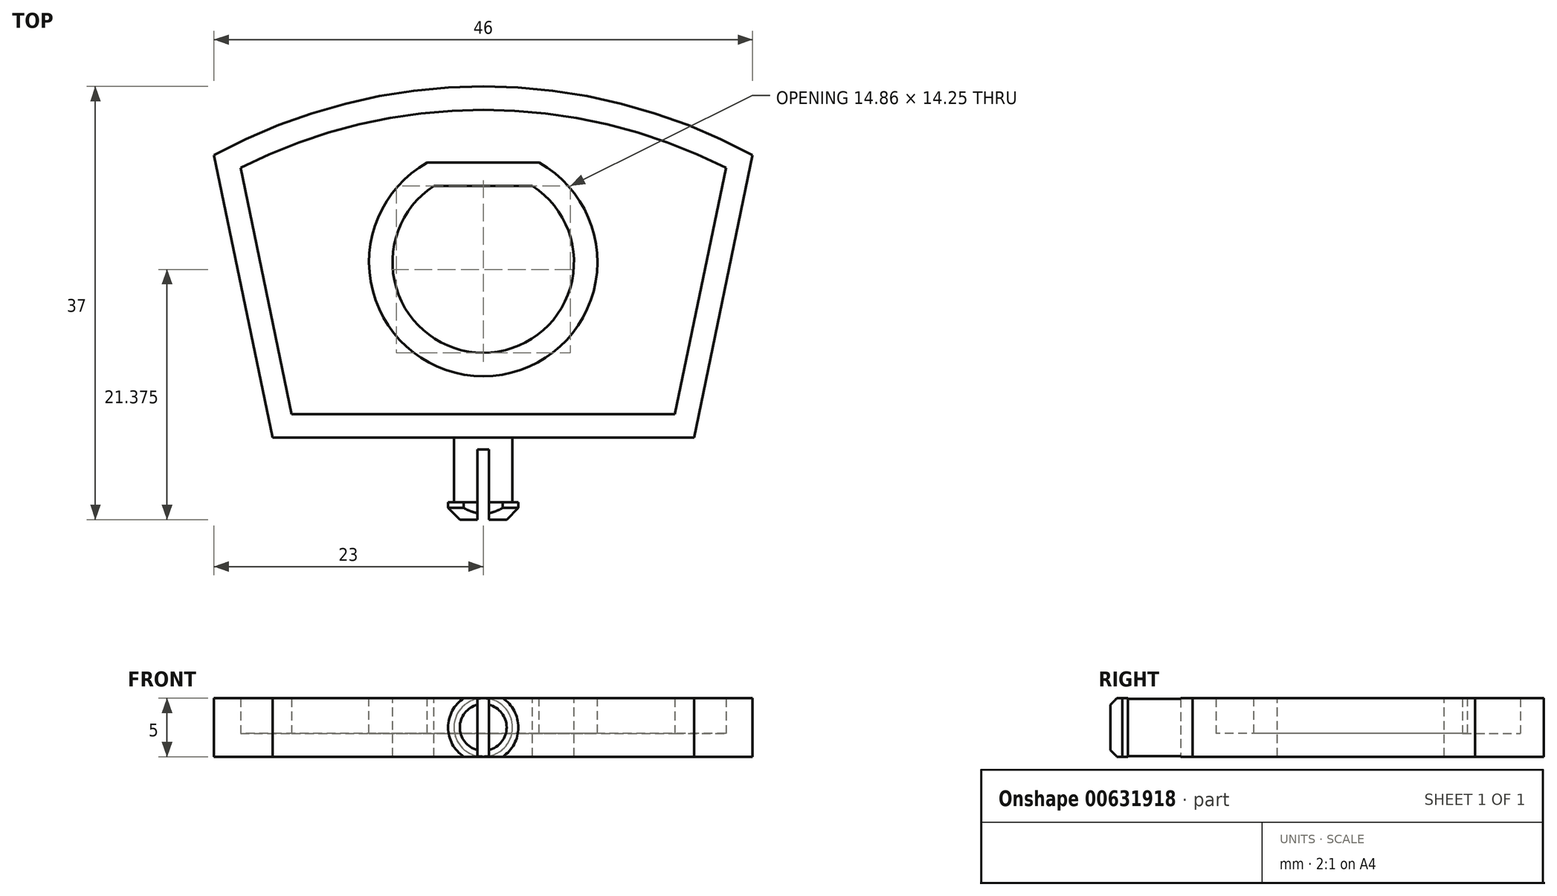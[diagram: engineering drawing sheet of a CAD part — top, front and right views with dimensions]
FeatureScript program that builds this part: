
annotation { "Feature Type Name" : "Feature", "Feature Type Description" : "" }
export const myFeature = defineFeature(function(context is Context, id is Id, definition is map)
    precondition{}
    {
        {
            var Q0;
            Q0=qCreatedBy(makeId("Top.planeOp"),FACE);
            var sketch = newSketch(context, id + "F0", { "sketchPlane" : qUnion([Q0])});
            skLineSegment(sketch, "E0", {"start": v(-23, 24.13) * mm, "end": v(-18, 0) * mm});
            skLineSegment(sketch, "E1", {"start": v(-18, 0) * mm, "end": v(18, 0) * mm});
            skLineSegment(sketch, "E2", {"start": v(18, 0) * mm, "end": v(23, 24.13) * mm});
            skArc(sketch, "E3", {"start": v(23, 24.13) * mm, "mid": v(0, 30) * mm, "end": v(-23, 24.13) * mm});
            skSolve(sketch);
        }
        {
            var Q0;
            Q0=makeQuery(id+"F0.imprint","IMPRINT",FACE,{"disambiguationData":[TD([[makeQuery(id+"F0.imprint","IMPRINT",EDGE,{"derivedFrom":sQuery(id+"F0.wireOp",EDGE,"E0")}),1.0]])]});
            extrude(context, id + "F1", {"entities" : qUnion([Q0]), "endBound" : BoundingType.SYMMETRIC, "depth" : 5 * mm, "offsetDistance" : 25 * mm});
        }
        {
            var Q0;
            Q0=makeQuery(id+"F1.opExtrude","CAP_FACE",FACE,{"disambiguationData":[OSD([sQuery(id+"F0.wireOp",EDGE,"E0"),sQuery(id+"F0.wireOp",EDGE,"E1"),sQuery(id+"F0.wireOp",EDGE,"E2"),sQuery(id+"F0.wireOp",EDGE,"E3")])],"isStart":false});
            var sketch = newSketch(context, id + "F2", { "sketchPlane" : qUnion([Q0])});
            skLineSegment(sketch, "E4", {"start": v(-4.22, 21.5) * mm, "end": v(4.22, 21.5) * mm});
            skArc(sketch, "E5", {"start": v(-4.22, 21.5) * mm, "mid": v(0, 7.25) * mm, "end": v(4.22, 21.5) * mm});
            skSolve(sketch);
        }
        {
            var Q0;
            Q0 = qSketchRegion(id + "F2", true);
            extrude(context, id + "F3", {"entities" : qUnion([Q0]), "operationType" : NewBodyOperationType.REMOVE, "endBound" : BoundingType.UP_TO_NEXT, "oppositeDirection" : true, "depth" : 25 * mm, "offsetDistance" : 25 * mm});
        }
        {
            var Q0;
            Q0=makeQuery(id+"F1.opExtrude","CAP_FACE",FACE,{"disambiguationData":[OSD([sQuery(id+"F0.wireOp",EDGE,"E0"),sQuery(id+"F0.wireOp",EDGE,"E1"),sQuery(id+"F0.wireOp",EDGE,"E2"),sQuery(id+"F0.wireOp",EDGE,"E3")])],"isStart":false});
            shell(context, id + "F4", {"entities" : qUnion([Q0]), "thickness" : 2 * mm});
        }
        {
            var Q0;
            Q0=qCreatedBy(makeId("Right.planeOp"),FACE);
            var sketch = newSketch(context, id + "F5", { "sketchPlane" : qUnion([Q0])});
            skLineSegment(sketch, "E6", {"start": v(0, 0) * mm, "end": v(-7, 0) * mm});
            skLineSegment(sketch, "E7", {"start": v(-7, 0) * mm, "end": v(-7, 3) * mm});
            skLineSegment(sketch, "E8", {"start": v(-7, 3) * mm, "end": v(-5.5, 3) * mm});
            skLineSegment(sketch, "E9", {"start": v(-5.5, 3) * mm, "end": v(-5.5, 2.5) * mm});
            skLineSegment(sketch, "E10", {"start": v(-5.5, 2.5) * mm, "end": v(0, 2.5) * mm});
            skLineSegment(sketch, "E11", {"start": v(0, 2.5) * mm, "end": v(0, 0) * mm});
            skSolve(sketch);
        }
        {
            var Q0;
            Q0=makeQuery(id+"F5.imprint","IMPRINT",FACE,{"disambiguationData":[TD([[makeQuery(id+"F5.imprint","IMPRINT",EDGE,{"derivedFrom":sQuery(id+"F5.wireOp",EDGE,"E6")}),-1.0]])]});
            var Q1;
            Q1=sQuery(id+"F5.wireOp",EDGE,"E6");
            revolve(context, id + "F6", {"operationType" : NewBodyOperationType.ADD, "entities" : qUnion([Q0]), "axis" : qUnion([Q1]), "revolveType" : RevolveType.FULL});
        }
        {
            var Q0;
            Q0=makeQuery(id+"F6.opRevolve","SWEPT_EDGE",EDGE,{"disambiguationData":[OSD([sQuery(id+"F5.wireOp",EDGE,"E7"),sQuery(id+"F5.wireOp",EDGE,"E8")])]});
            chamfer(context, id + "F7", {"entities" : qUnion([Q0]), "width" : 1 * mm, "tangentPropagation" : true});
        }
        {
            var Q0;
            Q0=makeQuery(id+"F6.opRevolve","SWEPT_FACE",FACE,{"disambiguationData":[OSD([sQuery(id+"F5.wireOp",EDGE,"E7")])]});
            var sketch = newSketch(context, id + "F8", { "sketchPlane" : qUnion([Q0])});
            skLineSegment(sketch, "E12.bottom", {"start": v(-23, 2.5) * mm, "end": v(23.2, 2.5) * mm});
            skLineSegment(sketch, "E12.top", {"start": v(-23, -2.5) * mm, "end": v(23.2, -2.5) * mm});
            skLineSegment(sketch, "E12.left", {"start": v(-23, 2.5) * mm, "end": v(-23, -2.5) * mm});
            skLineSegment(sketch, "E12.right", {"start": v(23.2, 2.5) * mm, "end": v(23.2, -2.5) * mm});
            skSolve(sketch);
        }
        {
            var Q0;
            Q0 = qSketchRegion(id + "F8", true);
            extrude(context, id + "F9", {"entities" : qUnion([Q0]), "operationType" : NewBodyOperationType.INTERSECT, "endBound" : BoundingType.THROUGH_ALL, "oppositeDirection" : true, "depth" : 25 * mm, "offsetDistance" : 25 * mm});
        }
        {
            var Q0;
            Q0=makeQuery(id+"F6.opRevolve","SWEPT_FACE",FACE,{"disambiguationData":[OSD([sQuery(id+"F5.wireOp",EDGE,"E7")])]});
            var sketch = newSketch(context, id + "F10", { "sketchPlane" : qUnion([Q0])});
            skLineSegment(sketch, "E13.bottom", {"start": v(-0.5, 3) * mm, "end": v(0.5, 3) * mm});
            skLineSegment(sketch, "E13.top", {"start": v(-0.5, -3) * mm, "end": v(0.5, -3) * mm});
            skLineSegment(sketch, "E13.left", {"start": v(-0.5, 3) * mm, "end": v(-0.5, -3) * mm});
            skLineSegment(sketch, "E13.right", {"start": v(0.5, 3) * mm, "end": v(0.5, -3) * mm});
            skSolve(sketch);
        }
        {
            var Q0;
            Q0 = qSketchRegion(id + "F10", true);
            extrude(context, id + "F11", {"entities" : qUnion([Q0]), "operationType" : NewBodyOperationType.REMOVE, "oppositeDirection" : true, "depth" : 6 * mm, "offsetDistance" : 25 * mm});
        }
    });
